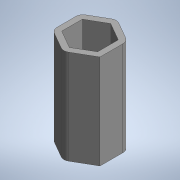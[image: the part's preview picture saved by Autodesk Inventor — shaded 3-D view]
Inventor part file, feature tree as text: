
AUTODESK INVENTOR PART (.ipt)
format: ipt  version: 2022.3 (Build 263350000, 350)  size: 92,672 bytes
history: native  units: mm (DEFAULTED — no unit token found)
features: extrude x1, fillet x1, sketch x1
ambient origin geometry x8: Origin, YZ Plane, XZ Plane, XY Plane, X Axis, Y Axis, Z Axis, Center Point
bodies: Solid1 (feature_tree)
feature tree (3):
  extrude  "Extrusion1"  Depth=9.652mm
  fillet  "Fillet1"  Radius=25.4mm
  sketch  "Sketch1"  dims[d0=12.7mm d2=9.652mm d3=25.4mm d4=0.0mm d5=2.0mm]
